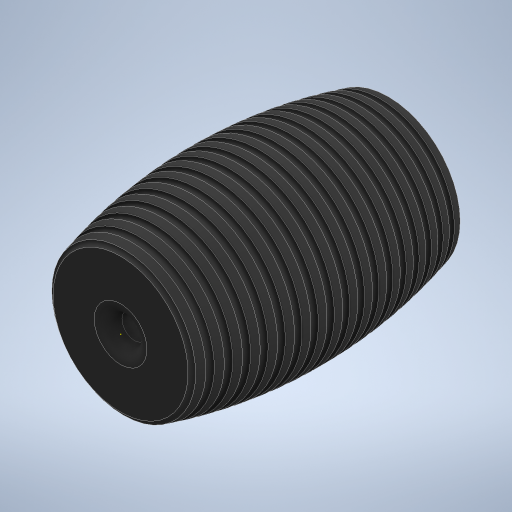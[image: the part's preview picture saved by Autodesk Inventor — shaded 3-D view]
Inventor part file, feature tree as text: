
AUTODESK INVENTOR PART (.ipt)
format: ipt  version: 2024.2 (Build 282272000, 272)  size: 586,240 bytes
history: native  units: mm
features: sketch x2, fillet x2, revolve x1
ambient origin geometry x8: Origin, YZ Plane, XZ Plane, XY Plane, X Axis, Y Axis, Z Axis, Center Point
bodies: Solid1 (feature_tree)
feature tree (5):
  revolve  "Revolution1"  [1 undecoded]
  sketch  "Sketch4"  dims[d4=360.0deg d5=0.5mm d6=2000.0mm d8=360.0deg d17=1.0mm d18=1.0mm d19=0.0mm d20=0.0mm d21=0.0mm]
  fillet  "Fillet1"  Radius=0.9mm
  fillet  "Fillet2"  Radius=35.0mm
  sketch  "Sketch1"  dims[d0=6.5mm d1=19.5mm d2=0.9mm d3=35.0mm]
note: 1 required parameter value undecoded (feature->parameter linkage not recoverable at this tier; creation-order binding heuristic only, values carry confidence <= 0.55)
